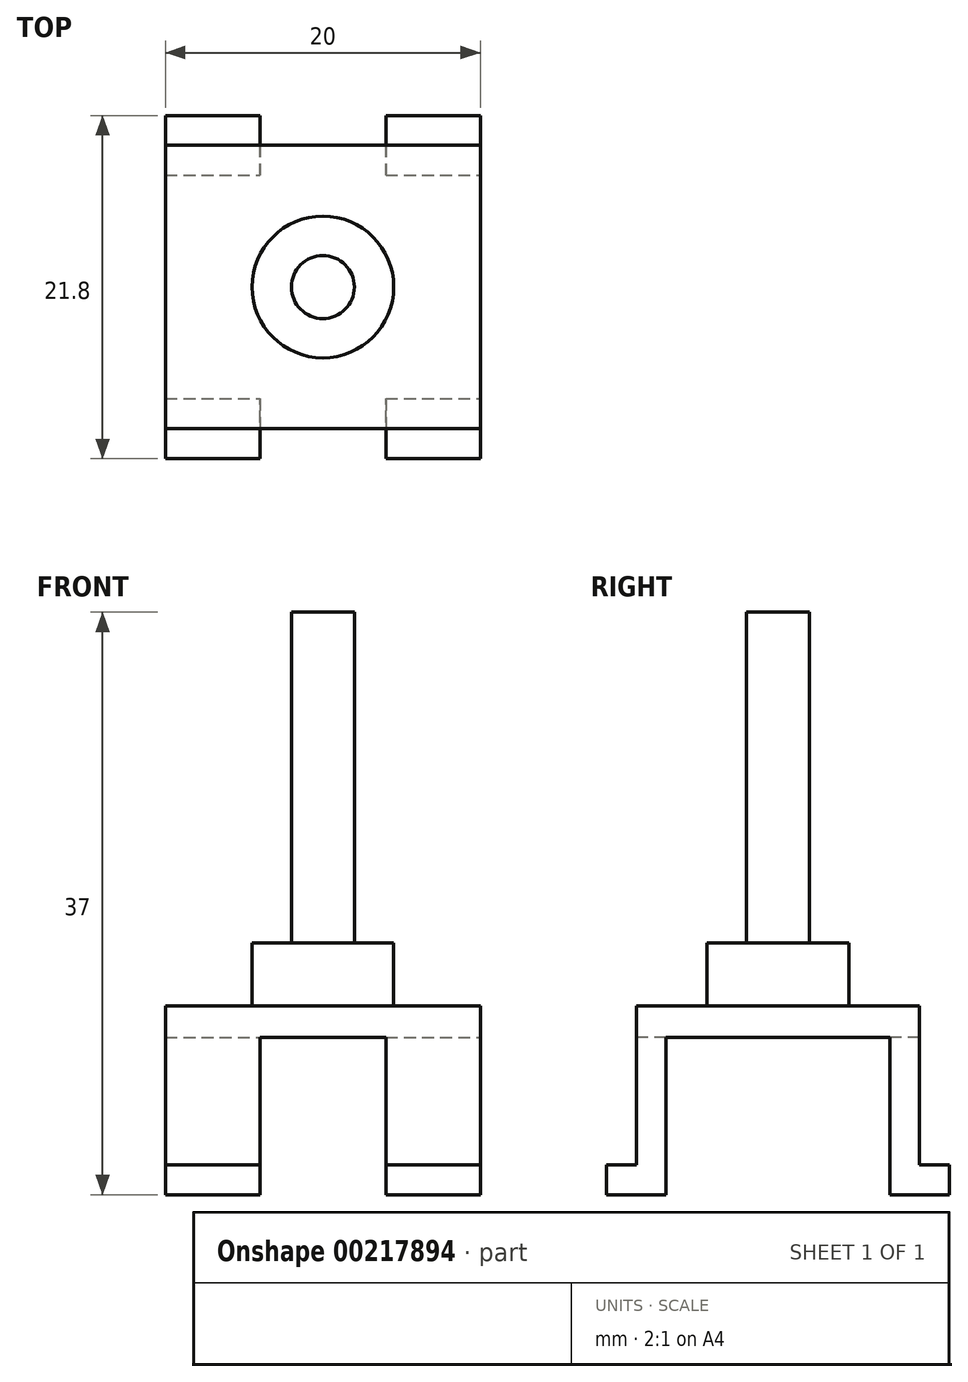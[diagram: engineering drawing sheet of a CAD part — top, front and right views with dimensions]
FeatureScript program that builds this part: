
annotation { "Feature Type Name" : "Feature", "Feature Type Description" : "" }
export const myFeature = defineFeature(function(context is Context, id is Id, definition is map)
    precondition{}
    {
        {
            var Q0;
            Q0=qCreatedBy(makeId("Top.planeOp"),FACE);
            var sketch = newSketch(context, id + "F0", { "sketchPlane" : qUnion([Q0])});
            skLineSegment(sketch, "E0.bottom", {"start": v(0, 0) * mm, "end": v(-20, 0) * mm});
            skLineSegment(sketch, "E0.top", {"start": v(0, 18) * mm, "end": v(-20, 18) * mm});
            skLineSegment(sketch, "E0.left", {"start": v(0, 0) * mm, "end": v(0, 18) * mm});
            skLineSegment(sketch, "E0.right", {"start": v(-20, 0) * mm, "end": v(-20, 18) * mm});
            skSolve(sketch);
        }
        {
            var Q0;
            Q0=makeQuery(id+"F0.imprint","IMPRINT",FACE,{"disambiguationData":[TD([[makeQuery(id+"F0.imprint","IMPRINT",EDGE,{"derivedFrom":sQuery(id+"F0.wireOp",EDGE,"E0.bottom")}),-1.0]])]});
            extrude(context, id + "F1", {"entities" : qUnion([Q0]), "depth" : 2 * mm});
        }
        {
            var Q0;
            Q0=makeQuery(id+"F1.opExtrude","CAP_FACE",FACE,{"disambiguationData":[OSD([sQuery(id+"F0.wireOp",EDGE,"E0.bottom"),sQuery(id+"F0.wireOp",EDGE,"E0.top"),sQuery(id+"F0.wireOp",EDGE,"E0.left"),sQuery(id+"F0.wireOp",EDGE,"E0.right")])],"isStart":true});
            var sketch = newSketch(context, id + "F2", { "sketchPlane" : qUnion([Q0])});
            skLineSegment(sketch, "E1.bottom", {"start": v(-20, 0) * mm, "end": v(0, 0) * mm});
            skLineSegment(sketch, "E1.top", {"start": v(-20, -1.9) * mm, "end": v(0, -1.9) * mm});
            skLineSegment(sketch, "E1.left", {"start": v(-20, 0) * mm, "end": v(-20, -1.9) * mm});
            skLineSegment(sketch, "E1.right", {"start": v(0, 0) * mm, "end": v(0, -1.9) * mm});
            skLineSegment(sketch, "E2", {"start": v(-20, -9) * mm, "end": v(-15.55, -9) * mm, "construction": true});
            skLineSegment(sketch, "E3.MirrorCS", {"start": v(-20, -16.1) * mm, "end": v(0, -16.1) * mm});
            skLineSegment(sketch, "E4.MirrorCS", {"start": v(-20, -18) * mm, "end": v(-20, -16.1) * mm});
            skLineSegment(sketch, "E5.MirrorCS", {"start": v(-20, -18) * mm, "end": v(0, -18) * mm});
            skLineSegment(sketch, "E6.MirrorCS", {"start": v(0, -18) * mm, "end": v(0, -16.1) * mm});
            skSolve(sketch);
        }
        {
            var Q0;
            Q0=makeQuery(id+"F2.imprint","IMPRINT",FACE,{"disambiguationData":[TD([[makeQuery(id+"F2.imprint","IMPRINT",EDGE,{"derivedFrom":sQuery(id+"F2.wireOp",EDGE,"E1.bottom")}),1.0]])]});
            var Q1;
            Q1=makeQuery(id+"F2.imprint","IMPRINT",FACE,{"disambiguationData":[TD([[makeQuery(id+"F2.imprint","IMPRINT",EDGE,{"derivedFrom":sQuery(id+"F2.wireOp",EDGE,"E3.MirrorCS")}),-1.0]])]});
            extrude(context, id + "F3", {"entities" : qUnion([Q0, Q1]), "operationType" : NewBodyOperationType.ADD, "depth" : 10 * mm});
        }
        {
            var Q0;
            Q0=makeQuery(id+"F3.boolean.opBoolean","MERGE",FACE,{"derivedFrom":[makeQuery(id+"F1.opExtrude","SWEPT_FACE",FACE,{"disambiguationData":[OSD([sQuery(id+"F0.wireOp",EDGE,"E0.bottom")])]}),makeQuery(id+"F3.opExtrude","SWEPT_FACE",FACE,{"disambiguationData":[OSD([sQuery(id+"F2.wireOp",EDGE,"E1.bottom")])]})]});
            var sketch = newSketch(context, id + "F4", { "sketchPlane" : qUnion([Q0])});
            skLineSegment(sketch, "E7.bottom", {"start": v(-20, -10) * mm, "end": v(0, -10) * mm});
            skLineSegment(sketch, "E7.top", {"start": v(-20, -8.1) * mm, "end": v(0, -8.1) * mm});
            skLineSegment(sketch, "E7.left", {"start": v(-20, -10) * mm, "end": v(-20, -8.1) * mm});
            skLineSegment(sketch, "E7.right", {"start": v(0, -10) * mm, "end": v(0, -8.1) * mm});
            skSolve(sketch);
        }
        {
            var Q0;
            Q0=makeQuery(id+"F4.imprint","IMPRINT",FACE,{"disambiguationData":[TD([[makeQuery(id+"F4.imprint","IMPRINT",EDGE,{"derivedFrom":sQuery(id+"F4.wireOp",EDGE,"E7.bottom")}),-1.0]])]});
            extrude(context, id + "F5", {"entities" : qUnion([Q0]), "operationType" : NewBodyOperationType.ADD, "depth" : 1.9 * mm});
        }
        {
            var Q0;
            Q0=makeQuery(id+"F3.boolean.opBoolean","MERGE",FACE,{"derivedFrom":[makeQuery(id+"F1.opExtrude","SWEPT_FACE",FACE,{"disambiguationData":[OSD([sQuery(id+"F0.wireOp",EDGE,"E0.top")])]}),makeQuery(id+"F3.opExtrude","SWEPT_FACE",FACE,{"disambiguationData":[OSD([sQuery(id+"F2.wireOp",EDGE,"E5.MirrorCS")])]})]});
            var sketch = newSketch(context, id + "F6", { "sketchPlane" : qUnion([Q0])});
            skLineSegment(sketch, "E8.bottom", {"start": v(0, -10) * mm, "end": v(20, -10) * mm});
            skLineSegment(sketch, "E8.top", {"start": v(0, -8.1) * mm, "end": v(20, -8.1) * mm});
            skLineSegment(sketch, "E8.left", {"start": v(0, -10) * mm, "end": v(0, -8.1) * mm});
            skLineSegment(sketch, "E8.right", {"start": v(20, -10) * mm, "end": v(20, -8.1) * mm});
            skSolve(sketch);
        }
        {
            var Q0;
            Q0=makeQuery(id+"F6.imprint","IMPRINT",FACE,{"disambiguationData":[TD([[makeQuery(id+"F6.imprint","IMPRINT",EDGE,{"derivedFrom":sQuery(id+"F6.wireOp",EDGE,"E8.bottom")}),1.0]])]});
            extrude(context, id + "F7", {"entities" : qUnion([Q0]), "operationType" : NewBodyOperationType.ADD, "depth" : 1.9 * mm});
        }
        {
            var Q0;
            Q0=makeQuery(id+"F1.opExtrude","CAP_FACE",FACE,{"disambiguationData":[OSD([sQuery(id+"F0.wireOp",EDGE,"E0.bottom"),sQuery(id+"F0.wireOp",EDGE,"E0.top"),sQuery(id+"F0.wireOp",EDGE,"E0.left"),sQuery(id+"F0.wireOp",EDGE,"E0.right")])],"isStart":false});
            var sketch = newSketch(context, id + "F8", { "sketchPlane" : qUnion([Q0])});
            skLineSegment(sketch, "E9", {"start": v(-10, 18) * mm, "end": v(-10, 0) * mm, "construction": true});
            skLineSegment(sketch, "E10", {"start": v(-20, 9) * mm, "end": v(-10, 9) * mm, "construction": true});
            skCircle(sketch, "E11", {"center": v(-10, 9) * mm, "radius": 4.5 * mm});
            skCircle(sketch, "E12", {"center": v(-10, 9) * mm, "radius": 2 * mm});
            skSolve(sketch);
        }
        {
            var Q0;
            Q0=makeQuery(id+"F8.imprint","IMPRINT",FACE,{"disambiguationData":[TD([[makeQuery(id+"F8.imprint","IMPRINT",EDGE,{"derivedFrom":sQuery(id+"F8.wireOp",EDGE,"E11")}),1.0]])]});
            extrude(context, id + "F9", {"entities" : qUnion([Q0]), "operationType" : NewBodyOperationType.ADD, "depth" : 4 * mm});
        }
        {
            var Q0;
            Q0=makeQuery(id+"F9.boolean.opBoolean","SPLIT",FACE,{"disambiguationData":[TD([makeQuery(id+"F9.opExtrude","SWEPT_FACE",FACE,{"disambiguationData":[OSD([sQuery(id+"F8.wireOp",EDGE,"E12")])]})])],"derivedFrom":makeQuery(id+"F1.opExtrude","CAP_FACE",FACE,{"disambiguationData":[OSD([sQuery(id+"F0.wireOp",EDGE,"E0.bottom"),sQuery(id+"F0.wireOp",EDGE,"E0.top"),sQuery(id+"F0.wireOp",EDGE,"E0.left"),sQuery(id+"F0.wireOp",EDGE,"E0.right")])],"isStart":false})});
            extrude(context, id + "F10", {"entities" : qUnion([Q0]), "operationType" : NewBodyOperationType.ADD, "depth" : 25 * mm});
        }
        {
            var Q0;
            Q0=makeQuery(id+"F3.boolean.opBoolean","MERGE",FACE,{"derivedFrom":[makeQuery(id+"F1.opExtrude","SWEPT_FACE",FACE,{"disambiguationData":[OSD([sQuery(id+"F0.wireOp",EDGE,"E0.bottom")])]}),makeQuery(id+"F3.opExtrude","SWEPT_FACE",FACE,{"disambiguationData":[OSD([sQuery(id+"F2.wireOp",EDGE,"E1.bottom")])]})]});
            var sketch = newSketch(context, id + "F11", { "sketchPlane" : qUnion([Q0])});
            skLineSegment(sketch, "E13", {"start": v(-20, 0) * mm, "end": v(-14, 0) * mm, "construction": true});
            skLineSegment(sketch, "E14", {"start": v(0, 0) * mm, "end": v(-6, 0) * mm, "construction": true});
            skLineSegment(sketch, "E15.bottom", {"start": v(-14, 0) * mm, "end": v(-6, 0) * mm});
            skLineSegment(sketch, "E15.top", {"start": v(-14, -12.69) * mm, "end": v(-6, -12.69) * mm});
            skLineSegment(sketch, "E15.left", {"start": v(-14, 0) * mm, "end": v(-14, -12.69) * mm});
            skLineSegment(sketch, "E15.right", {"start": v(-6, 0) * mm, "end": v(-6, -12.69) * mm});
            skSolve(sketch);
        }
        {
            var Q0;
            {var subQ0=sQuery(id+"F11.wireOp",EDGE,"E15.bottom");Q0=makeQuery(id+"F11.imprint","IMPRINT",FACE,{"disambiguationData":[TD([[makeQuery(id+"F11.imprint","IMPRINT",EDGE,{"derivedFrom":subQ0}),-1.0]])]});}
            var Q1;
            {var subQ0=sQuery(id+"F11.wireOp",EDGE,"E15.top");Q1=makeQuery(id+"F11.imprint","IMPRINT",FACE,{"disambiguationData":[TD([[makeQuery(id+"F11.imprint","IMPRINT",EDGE,{"derivedFrom":subQ0}),1.0]])]});}
            extrude(context, id + "F12", {"entities" : qUnion([Q0, Q1]), "operationType" : NewBodyOperationType.REMOVE, "endBound" : BoundingType.THROUGH_ALL, "oppositeDirection" : true, "depth" : 25 * mm, "hasSecondDirection" : true, "secondDirectionOppositeDirection" : false, "secondDirectionDepth" : 25 * mm});
        }
    });
